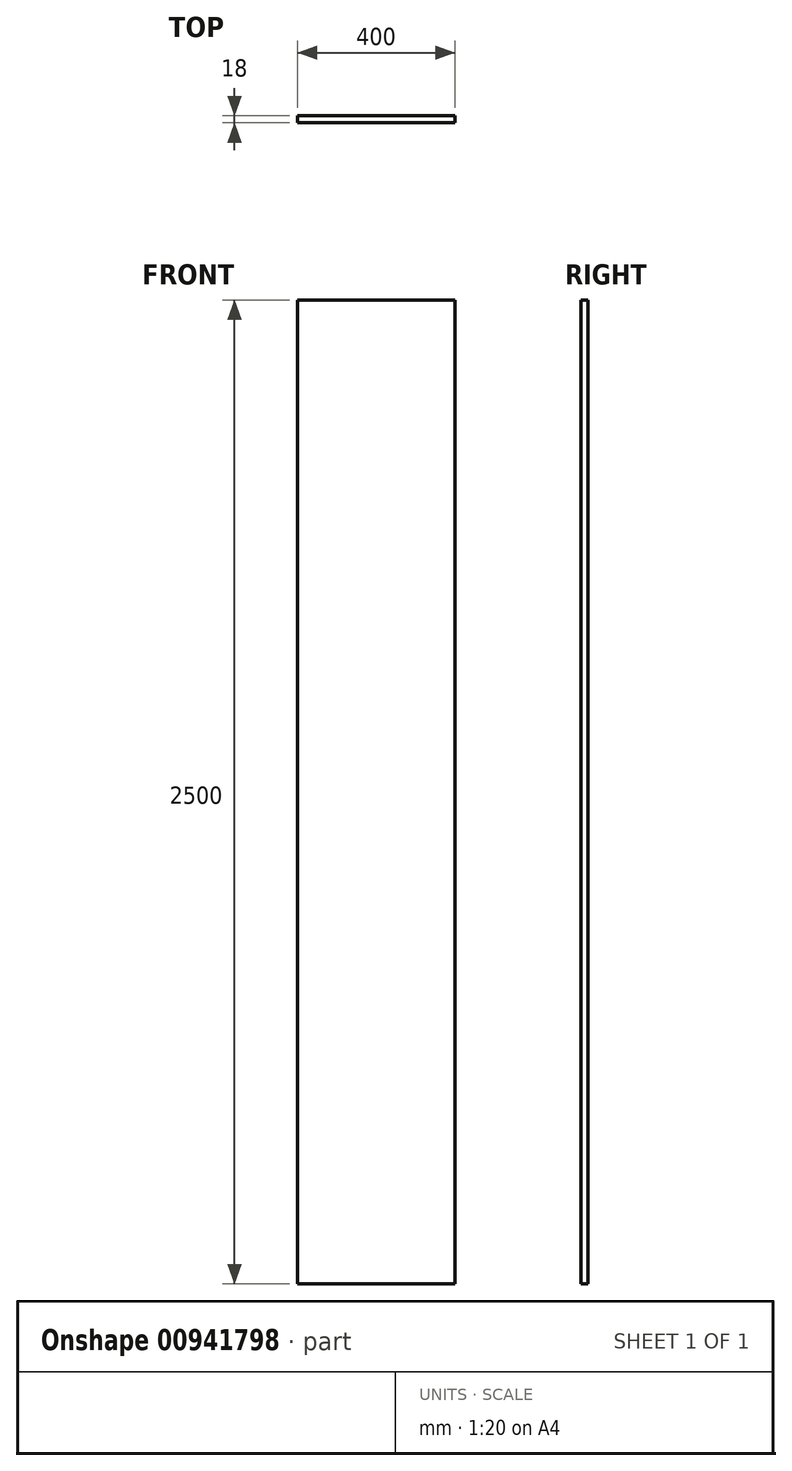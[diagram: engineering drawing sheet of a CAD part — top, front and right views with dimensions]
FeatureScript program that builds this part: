
annotation { "Feature Type Name" : "Feature", "Feature Type Description" : "" }
export const myFeature = defineFeature(function(context is Context, id is Id, definition is map)
    precondition{}
    {
        {
            var Q0;
            Q0=qCreatedBy(makeId("Front.planeOp"),FACE);
            var sketch = newSketch(context, id + "F0", { "sketchPlane" : qUnion([Q0])});
            skLineSegment(sketch, "E0.bottom", {"start": v(200, 1250) * mm, "end": v(-200, 1250) * mm});
            skLineSegment(sketch, "E0.top", {"start": v(200, -1250) * mm, "end": v(-200, -1250) * mm});
            skLineSegment(sketch, "E0.left", {"start": v(200, 1250) * mm, "end": v(200, -1250) * mm});
            skLineSegment(sketch, "E0.right", {"start": v(-200, 1250) * mm, "end": v(-200, -1250) * mm});
            skPoint(sketch, "E0.middle", {"position": v(0, 0) * mm});
            skSolve(sketch);
        }
        {
            var Q0;
            Q0 = qSketchRegion(id + "F0", true);
            extrude(context, id + "F1", {"entities" : qUnion([Q0]), "endBound" : BoundingType.SYMMETRIC, "depth" : 18 * mm, "offsetDistance" : 25 * mm});
        }
    });
